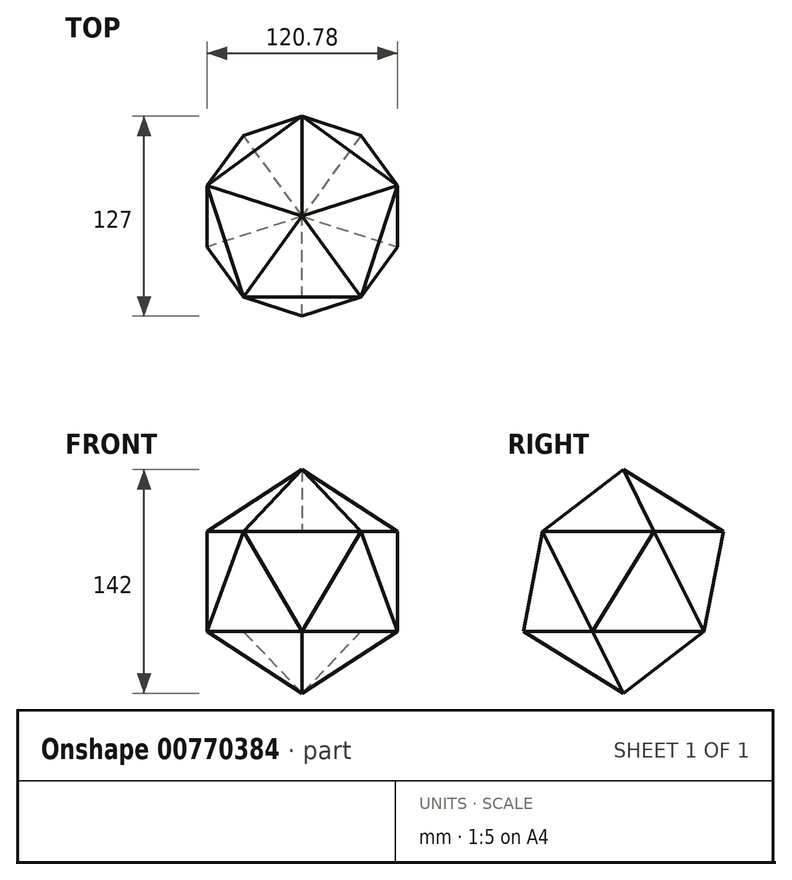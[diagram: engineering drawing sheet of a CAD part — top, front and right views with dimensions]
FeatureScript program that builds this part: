
annotation { "Feature Type Name" : "Feature", "Feature Type Description" : "" }
export const myFeature = defineFeature(function(context is Context, id is Id, definition is map)
    precondition{}
    {
        {
            var Q0;
            Q0=qCreatedBy(makeId("Top.planeOp"),FACE);
            var sketch = newSketch(context, id + "F0", { "sketchPlane" : qUnion([Q0])});
            skCircle(sketch, "E0", {"center": v(37.32, 51.37) * mm, "radius": 74.65 * mm});
            skCircle(sketch, "E1", {"center": v(-37.32, 51.37) * mm, "radius": 74.65 * mm});
            skCircle(sketch, "E2", {"center": v(0, 51.37) * mm, "radius": 64.65 * mm});
            skLineSegment(sketch, "E3", {"start": v(0, 0) * mm, "end": v(39.25, 0) * mm});
            skLineSegment(sketch, "E4", {"start": v(0, 63.5) * mm, "end": v(-63.5, 63.5) * mm});
            skCircle(sketch, "E5", {"center": v(0, 0) * mm, "radius": 63.5 * mm});
            skLineSegment(sketch, "E6", {"start": v(0, 0) * mm, "end": v(0, -63.5) * mm});
            skLineSegment(sketch, "E7", {"start": v(-37.32, 51.37) * mm, "end": v(37.32, 51.37) * mm});
            skLineSegment(sketch, "E8", {"start": v(37.32, 51.37) * mm, "end": v(60.4, -19.62) * mm});
            skLineSegment(sketch, "E9", {"start": v(60.4, -19.62) * mm, "end": v(0, -63.5) * mm});
            skLineSegment(sketch, "E10", {"start": v(0, -63.5) * mm, "end": v(-60.4, -19.62) * mm});
            skLineSegment(sketch, "E11", {"start": v(-60.4, -19.62) * mm, "end": v(-37.32, 51.37) * mm});
            skLineSegment(sketch, "E12", {"start": v(0, 63.5) * mm, "end": v(0, 116.02) * mm});
            skSolve(sketch);
        }
        {
            var Q0;
            Q0=sQuery(id+"F0.wireOp",EDGE,"E4");
            cPlane(context, id + "F1", {"entities" : qUnion([Q0]), "cplaneType" : CPlaneType.LINE_ANGLE, "offset" : 25.4 * mm, "angle" : 180 * degree, "width" : 152.4 * mm, "height" : 152.4 * mm});
        }
        {
            var Q0;
            Q0=qCreatedBy(id+"F1.planeOp",FACE);
            var sketch = newSketch(context, id + "F2", { "sketchPlane" : qUnion([Q0])});
            skLineSegment(sketch, "E13", {"start": v(63.5, 0) * mm, "end": v(0, 0) * mm});
            skLineSegment(sketch, "E14", {"start": v(31.75, 0) * mm, "end": v(63.5, 31.75) * mm});
            skLineSegment(sketch, "E15", {"start": v(31.75, 0) * mm, "end": v(0, -31.75) * mm});
            skLineSegment(sketch, "E16", {"start": v(63.5, 31.75) * mm, "end": v(0, 31.75) * mm});
            skLineSegment(sketch, "E17", {"start": v(0, -31.75) * mm, "end": v(63.5, -31.75) * mm});
            skLineSegment(sketch, "E18", {"start": v(0, 0) * mm, "end": v(0, 31.75) * mm});
            skLineSegment(sketch, "E19", {"start": v(0, 0) * mm, "end": v(0, -31.75) * mm});
            skSolve(sketch);
        }
        {
            var Q0;
            Q0=sQuery(id+"F2.wireOp",EDGE,"E16");
            cPlane(context, id + "F3", {"entities" : qUnion([Q0]), "cplaneType" : CPlaneType.LINE_ANGLE, "offset" : 25.4 * mm, "angle" : 270 * degree, "width" : 152.4 * mm, "height" : 152.4 * mm});
        }
        {
            var Q0;
            Q0=qCreatedBy(id+"F3.planeOp",FACE);
            var sketch = newSketch(context, id + "F4", { "sketchPlane" : qUnion([Q0])});
            skCircle(sketch, "E20.0", {"center": v(0, 0) * mm, "radius": 63.5 * mm});
            skLineSegment(sketch, "E21", {"start": v(-37.32, 51.37) * mm, "end": v(37.32, 51.37) * mm});
            skLineSegment(sketch, "E22", {"start": v(37.32, 51.37) * mm, "end": v(60.4, -19.62) * mm});
            skLineSegment(sketch, "E23", {"start": v(60.4, -19.62) * mm, "end": v(0, -63.5) * mm});
            skLineSegment(sketch, "E24", {"start": v(0, -63.5) * mm, "end": v(-60.4, -19.62) * mm});
            skLineSegment(sketch, "E25", {"start": v(-60.4, -19.62) * mm, "end": v(-37.32, 51.37) * mm});
            skLineSegment(sketch, "E26", {"start": v(0, 51.37) * mm, "end": v(0, 63.5) * mm});
            skLineSegment(sketch, "E27", {"start": v(30.2, -41.56) * mm, "end": v(37.32, -51.37) * mm});
            skLineSegment(sketch, "E28", {"start": v(37.32, -51.37) * mm, "end": v(60.4, -19.62) * mm});
            skLineSegment(sketch, "E29", {"start": v(37.32, -51.37) * mm, "end": v(0, -63.5) * mm});
            skLineSegment(sketch, "E30", {"start": v(-30.2, -41.56) * mm, "end": v(-37.32, -51.37) * mm});
            skLineSegment(sketch, "E31", {"start": v(-37.32, -51.37) * mm, "end": v(0, -63.5) * mm});
            skLineSegment(sketch, "E32", {"start": v(-37.32, -51.37) * mm, "end": v(-60.4, -19.62) * mm});
            skLineSegment(sketch, "E33", {"start": v(-48.86, 15.87) * mm, "end": v(-60.4, 19.62) * mm});
            skLineSegment(sketch, "E34", {"start": v(-60.4, 19.62) * mm, "end": v(-60.4, -19.62) * mm});
            skLineSegment(sketch, "E35", {"start": v(-60.4, 19.62) * mm, "end": v(-37.32, 51.37) * mm});
            skLineSegment(sketch, "E36", {"start": v(-37.32, 51.37) * mm, "end": v(0, 63.5) * mm});
            skLineSegment(sketch, "E37", {"start": v(0, 63.5) * mm, "end": v(37.32, 51.37) * mm});
            skLineSegment(sketch, "E38", {"start": v(60.4, 19.62) * mm, "end": v(37.32, 51.37) * mm});
            skLineSegment(sketch, "E39", {"start": v(60.4, 19.62) * mm, "end": v(60.4, -19.62) * mm});
            skLineSegment(sketch, "E40", {"start": v(48.86, 15.87) * mm, "end": v(60.4, 19.62) * mm});
            skLineSegment(sketch, "E41", {"start": v(0, 0) * mm, "end": v(30.2, -41.56) * mm});
            skLineSegment(sketch, "E42", {"start": v(0, 0) * mm, "end": v(-30.2, -41.56) * mm});
            skLineSegment(sketch, "E43", {"start": v(0, 0) * mm, "end": v(-48.86, 15.87) * mm});
            skLineSegment(sketch, "E44", {"start": v(0, 0) * mm, "end": v(48.86, 15.87) * mm});
            skLineSegment(sketch, "E45", {"start": v(0, 0) * mm, "end": v(0, 51.37) * mm});
            skSolve(sketch);
        }
        {
            var Q0;
            Q0=sQuery(id+"F2.wireOp",EDGE,"E17");
            cPlane(context, id + "F5", {"entities" : qUnion([Q0]), "cplaneType" : CPlaneType.LINE_ANGLE, "offset" : 25.4 * mm, "angle" : 90 * degree, "width" : 152.4 * mm, "height" : 152.4 * mm});
        }
        {
            var Q0;
            Q0=qCreatedBy(id+"F5.planeOp",FACE);
            var sketch = newSketch(context, id + "F6", { "sketchPlane" : qUnion([Q0])});
            skCircle(sketch, "E46.0", {"center": v(0, 0) * mm, "radius": 63.5 * mm});
            skLineSegment(sketch, "E47", {"start": v(-37.32, 51.37) * mm, "end": v(37.32, 51.37) * mm});
            skLineSegment(sketch, "E48", {"start": v(37.32, 51.37) * mm, "end": v(60.4, -19.62) * mm});
            skLineSegment(sketch, "E49", {"start": v(60.4, -19.62) * mm, "end": v(0, -63.5) * mm});
            skLineSegment(sketch, "E50", {"start": v(0, -63.5) * mm, "end": v(-60.4, -19.62) * mm});
            skLineSegment(sketch, "E51", {"start": v(-60.4, -19.62) * mm, "end": v(-37.32, 51.37) * mm});
            skLineSegment(sketch, "E52", {"start": v(0, 51.37) * mm, "end": v(0, 63.5) * mm});
            skLineSegment(sketch, "E53", {"start": v(30.2, -41.56) * mm, "end": v(37.32, -51.37) * mm});
            skLineSegment(sketch, "E54", {"start": v(37.32, -51.37) * mm, "end": v(60.4, -19.62) * mm});
            skLineSegment(sketch, "E55", {"start": v(37.32, -51.37) * mm, "end": v(0, -63.5) * mm});
            skLineSegment(sketch, "E56", {"start": v(-30.2, -41.56) * mm, "end": v(-37.32, -51.37) * mm});
            skLineSegment(sketch, "E57", {"start": v(-37.32, -51.37) * mm, "end": v(0, -63.5) * mm});
            skLineSegment(sketch, "E58", {"start": v(-37.32, -51.37) * mm, "end": v(-60.4, -19.62) * mm});
            skLineSegment(sketch, "E59", {"start": v(-48.86, 15.87) * mm, "end": v(-60.4, 19.62) * mm});
            skLineSegment(sketch, "E60", {"start": v(-60.4, 19.62) * mm, "end": v(-60.4, -19.62) * mm});
            skLineSegment(sketch, "E61", {"start": v(-60.4, 19.62) * mm, "end": v(-37.32, 51.37) * mm});
            skLineSegment(sketch, "E62", {"start": v(-37.32, 51.37) * mm, "end": v(0, 63.5) * mm});
            skLineSegment(sketch, "E63", {"start": v(0, 63.5) * mm, "end": v(37.32, 51.37) * mm});
            skLineSegment(sketch, "E64", {"start": v(60.4, 19.62) * mm, "end": v(37.32, 51.37) * mm});
            skLineSegment(sketch, "E65", {"start": v(60.4, 19.62) * mm, "end": v(60.4, -19.62) * mm});
            skLineSegment(sketch, "E66", {"start": v(48.86, 15.87) * mm, "end": v(60.4, 19.62) * mm});
            skLineSegment(sketch, "E67", {"start": v(0, 0) * mm, "end": v(30.2, -41.56) * mm});
            skLineSegment(sketch, "E68", {"start": v(0, 0) * mm, "end": v(-30.2, -41.56) * mm});
            skLineSegment(sketch, "E69", {"start": v(0, 0) * mm, "end": v(-48.86, 15.88) * mm});
            skLineSegment(sketch, "E70", {"start": v(0, 0) * mm, "end": v(48.86, 15.87) * mm});
            skLineSegment(sketch, "E71", {"start": v(0, 0) * mm, "end": v(0, 51.37) * mm});
            skLineSegment(sketch, "E72.0", {"start": v(-60.4, -19.62) * mm, "end": v(-60.4, 19.62) * mm, "construction": true});
            skLineSegment(sketch, "E73", {"start": v(63.5, 0) * mm, "end": v(74.27, 0) * mm});
            skPoint(sketch, "E73.startSnap0", {"position": v(60.4, 0) * mm});
            skSolve(sketch);
        }
        {
            var Q0;
            Q0=qCreatedBy(makeId("Front.planeOp"),FACE);
            var sketch = newSketch(context, id + "F7", { "sketchPlane" : qUnion([Q0])});
            skLineSegment(sketch, "E74", {"start": v(39.25, 31.75) * mm, "end": v(0, 31.75) * mm});
            skLineSegment(sketch, "E75", {"start": v(39.25, 31.75) * mm, "end": v(0, 71) * mm});
            skLineSegment(sketch, "E76", {"start": v(0, -31.75) * mm, "end": v(39.25, -31.75) * mm});
            skLineSegment(sketch, "E77", {"start": v(39.25, -31.75) * mm, "end": v(0, -71) * mm});
            skLineSegment(sketch, "E78", {"start": v(39.25, -31.75) * mm, "end": v(63.5, -31.75) * mm});
            skLineSegment(sketch, "E79", {"start": v(63.5, -31.75) * mm, "end": v(0, 0) * mm});
            skCircle(sketch, "E80", {"center": v(0, 0) * mm, "radius": 71 * mm});
            skLineSegment(sketch, "E81", {"start": v(0, 0) * mm, "end": v(0, -71) * mm});
            skLineSegment(sketch, "E82", {"start": v(0, 0) * mm, "end": v(0, 71) * mm});
            skLineSegment(sketch, "E83", {"start": v(39.25, 31.75) * mm, "end": v(71, 0) * mm});
            skLineSegment(sketch, "E84", {"start": v(0, 0) * mm, "end": v(39.25, 0) * mm});
            skLineSegment(sketch, "E85", {"start": v(39.25, 0) * mm, "end": v(39.25, 31.75) * mm});
            skSolve(sketch);
        }
        {
            var Q0;
            Q0=qCreatedBy(makeId("Top.planeOp"),FACE);
            var sketch = newSketch(context, id + "F8", { "sketchPlane" : qUnion([Q0])});
            skLineSegment(sketch, "E86", {"start": v(0, 0) * mm, "end": v(71, 0) * mm});
            skCircle(sketch, "E87", {"center": v(0, 0) * mm, "radius": 71 * mm});
            skLineSegment(sketch, "E88", {"start": v(0, 0) * mm, "end": v(67.52, -21.94) * mm});
            skLineSegment(sketch, "E89", {"start": v(0, 0) * mm, "end": v(67.52, 21.94) * mm});
            skLineSegment(sketch, "E90", {"start": v(0, 0) * mm, "end": v(41.73, 57.44) * mm});
            skLineSegment(sketch, "E91", {"start": v(0, 0) * mm, "end": v(0, 71) * mm});
            skLineSegment(sketch, "E92", {"start": v(0, 0) * mm, "end": v(41.73, -57.44) * mm});
            skLineSegment(sketch, "E93", {"start": v(0, 0) * mm, "end": v(0, -71) * mm});
            skLineSegment(sketch, "E94", {"start": v(0, 0) * mm, "end": v(-41.73, -57.44) * mm});
            skLineSegment(sketch, "E95", {"start": v(0, 0) * mm, "end": v(-41.73, 57.44) * mm});
            skLineSegment(sketch, "E96", {"start": v(0, 0) * mm, "end": v(-67.52, 21.94) * mm});
            skLineSegment(sketch, "E97", {"start": v(0, 0) * mm, "end": v(-67.52, -21.94) * mm});
            skSolve(sketch);
        }
        {
            var Q0;
            {var subQ0=sQuery(id+"F7.wireOp",EDGE,"E81");var subQ1=makeQuery(id+"F7.imprint","INTERSECT",VERTEX,{"derivedFrom":[sQuery(id+"F7.wireOp",EDGE,"E76"),subQ0]});Q0=makeQuery(id+"F7.imprint","IMPRINT",FACE,{"disambiguationData":[TD([[makeQuery(id+"F7.imprint","IMPRINT",EDGE,{"disambiguationData":[TD([[subQ1,1.0]])],"derivedFrom":subQ0}),-1.0]])]});}
            var Q1;
            Q1=sQuery(id+"F7.wireOp",EDGE,"E81");
            revolve(context, id + "F9", {"surfaceOperationType" : NewSurfaceOperationType.NEW, "entities" : qUnion([Q0]), "axis" : qUnion([Q1]), "revolveType" : RevolveType.FULL});
        }
        {
            var Q0;
            Q0=sQuery(id+"F6.wireOp",VERTEX,"E53.end");
            var Q1;
            Q1=sQuery(id+"F6.wireOp",VERTEX,"E67.start");
            var Q2;
            Q2=sQuery(id+"F7.wireOp",VERTEX,"E77.end");
            cPlane(context, id + "F10", {"entities" : qUnion([Q0, Q1, Q2]), "cplaneType" : CPlaneType.THREE_POINT, "offset" : 25.4 * mm, "width" : 152.4 * mm, "height" : 152.4 * mm});
        }
        {
            var Q0;
            Q0=qCreatedBy(id+"F10.planeOp",FACE);
            var sketch = newSketch(context, id + "F11", { "sketchPlane" : qUnion([Q0])});
            skLineSegment(sketch, "E98", {"start": v(0, -71) * mm, "end": v(-51.37, -31.75) * mm});
            skLineSegment(sketch, "E99", {"start": v(-51.37, -31.75) * mm, "end": v(-63.5, -31.75) * mm});
            skLineSegment(sketch, "E100", {"start": v(-63.5, -31.75) * mm, "end": v(-63.5, -71) * mm});
            skLineSegment(sketch, "E101", {"start": v(-63.5, -71) * mm, "end": v(0, -71) * mm});
            skSolve(sketch);
        }
        {
            var Q0;
            {var subQ0=sQuery(id+"F11.wireOp",EDGE,"E98");Q0=makeQuery(id+"F11.imprint","IMPRINT",FACE,{"disambiguationData":[TD([[makeQuery(id+"F11.imprint","IMPRINT",EDGE,{"derivedFrom":subQ0}),1.0]])]});}
            var Q1;
            Q1=sQuery(id+"F6.wireOp",VERTEX,"E48.end");
            var Q2;
            Q2=sQuery(id+"F6.wireOp",VERTEX,"E49.end");
            extrude(context, id + "F12", {"entities" : qUnion([Q0]), "operationType" : NewBodyOperationType.REMOVE, "endBound" : BoundingType.UP_TO_VERTEX, "depth" : 25.4 * mm, "endBoundEntityVertex" : qUnion([Q1]), "offsetDistance" : 25.4 * mm, "hasSecondDirection" : true, "secondDirectionBound" : SecondDirectionBoundingType.UP_TO_VERTEX, "secondDirectionOppositeDirection" : true, "secondDirectionDepth" : 25.4 * mm, "secondDirectionBoundEntityVertex" : qUnion([Q2])});
        }
        {
            var Q0;
            Q0=sQuery(id+"F7.wireOp",VERTEX,"E77.end");
            var Q1;
            Q1=sQuery(id+"F6.wireOp",VERTEX,"E67.start");
            var Q2;
            Q2=sQuery(id+"F6.wireOp",VERTEX,"E56.end");
            cPlane(context, id + "F13", {"entities" : qUnion([Q0, Q1, Q2]), "cplaneType" : CPlaneType.THREE_POINT, "offset" : 25.4 * mm, "width" : 152.4 * mm, "height" : 152.4 * mm});
        }
        {
            var Q0;
            Q0=qCreatedBy(id+"F13.planeOp",FACE);
            var sketch = newSketch(context, id + "F14", { "sketchPlane" : qUnion([Q0])});
            skLineSegment(sketch, "E102", {"start": v(0, -71) * mm, "end": v(51.37, -31.75) * mm});
            skLineSegment(sketch, "E103", {"start": v(0, -71) * mm, "end": v(63.5, -71) * mm});
            skLineSegment(sketch, "E104", {"start": v(63.5, -71) * mm, "end": v(63.5, -31.75) * mm});
            skLineSegment(sketch, "E105", {"start": v(63.5, -31.75) * mm, "end": v(51.37, -31.75) * mm});
            skSolve(sketch);
        }
        {
            var Q0;
            {var subQ0=sQuery(id+"F14.wireOp",EDGE,"E102");Q0=makeQuery(id+"F14.imprint","IMPRINT",FACE,{"disambiguationData":[TD([[makeQuery(id+"F14.imprint","IMPRINT",EDGE,{"derivedFrom":subQ0}),-1.0]])]});}
            var Q1;
            Q1=sQuery(id+"F6.wireOp",VERTEX,"E49.end");
            var Q2;
            Q2=sQuery(id+"F6.wireOp",VERTEX,"E50.end");
            extrude(context, id + "F15", {"entities" : qUnion([Q0]), "operationType" : NewBodyOperationType.REMOVE, "endBound" : BoundingType.UP_TO_VERTEX, "oppositeDirection" : true, "depth" : 25.4 * mm, "endBoundEntityVertex" : qUnion([Q1]), "offsetDistance" : 25.4 * mm, "hasSecondDirection" : true, "secondDirectionBound" : SecondDirectionBoundingType.UP_TO_VERTEX, "secondDirectionOppositeDirection" : false, "secondDirectionDepth" : 25.4 * mm, "secondDirectionBoundEntityVertex" : qUnion([Q2])});
        }
        {
            var Q0;
            Q0=sQuery(id+"F6.wireOp",VERTEX,"E67.start");
            var Q1;
            Q1=sQuery(id+"F7.wireOp",VERTEX,"E77.end");
            var Q2;
            Q2=sQuery(id+"F6.wireOp",VERTEX,"E59.end");
            cPlane(context, id + "F16", {"entities" : qUnion([Q0, Q1, Q2]), "cplaneType" : CPlaneType.THREE_POINT, "offset" : 25.4 * mm, "width" : 152.4 * mm, "height" : 152.4 * mm});
        }
        {
            var Q0;
            Q0=qCreatedBy(id+"F16.planeOp",FACE);
            var sketch = newSketch(context, id + "F17", { "sketchPlane" : qUnion([Q0])});
            skLineSegment(sketch, "E106", {"start": v(0, -71) * mm, "end": v(-51.37, -31.75) * mm});
            skLineSegment(sketch, "E107", {"start": v(0, -71) * mm, "end": v(-63.5, -71) * mm});
            skLineSegment(sketch, "E108", {"start": v(-63.5, -71) * mm, "end": v(-63.5, -31.75) * mm});
            skLineSegment(sketch, "E109", {"start": v(-63.5, -31.75) * mm, "end": v(-51.37, -31.75) * mm});
            skSolve(sketch);
        }
        {
            var Q0;
            {var subQ0=sQuery(id+"F17.wireOp",EDGE,"E106");Q0=makeQuery(id+"F17.imprint","IMPRINT",FACE,{"disambiguationData":[TD([[makeQuery(id+"F17.imprint","IMPRINT",EDGE,{"derivedFrom":subQ0}),1.0]])]});}
            var Q1;
            Q1=sQuery(id+"F6.wireOp",VERTEX,"E47.start");
            var Q2;
            Q2=sQuery(id+"F6.wireOp",VERTEX,"E50.end");
            extrude(context, id + "F18", {"entities" : qUnion([Q0]), "operationType" : NewBodyOperationType.REMOVE, "endBound" : BoundingType.UP_TO_VERTEX, "oppositeDirection" : true, "depth" : 25.4 * mm, "endBoundEntityVertex" : qUnion([Q1]), "offsetDistance" : 25.4 * mm, "hasSecondDirection" : true, "secondDirectionBound" : SecondDirectionBoundingType.UP_TO_VERTEX, "secondDirectionOppositeDirection" : false, "secondDirectionDepth" : 25.4 * mm, "secondDirectionBoundEntityVertex" : qUnion([Q2])});
        }
        {
            var Q0;
            Q0=sQuery(id+"F7.wireOp",VERTEX,"E77.end");
            var Q1;
            Q1=sQuery(id+"F6.wireOp",VERTEX,"E67.start");
            var Q2;
            Q2=sQuery(id+"F6.wireOp",VERTEX,"E52.end");
            cPlane(context, id + "F19", {"entities" : qUnion([Q0, Q1, Q2]), "cplaneType" : CPlaneType.THREE_POINT, "offset" : 25.4 * mm, "width" : 152.4 * mm, "height" : 152.4 * mm});
        }
        {
            var Q0;
            Q0=qCreatedBy(id+"F19.planeOp",FACE);
            var sketch = newSketch(context, id + "F20", { "sketchPlane" : qUnion([Q0])});
            skLineSegment(sketch, "E110", {"start": v(0, -71) * mm, "end": v(51.37, -31.75) * mm});
            skLineSegment(sketch, "E111", {"start": v(0, -71) * mm, "end": v(63.5, -71) * mm});
            skLineSegment(sketch, "E112", {"start": v(63.5, -71) * mm, "end": v(63.5, -31.75) * mm});
            skLineSegment(sketch, "E113", {"start": v(63.5, -31.75) * mm, "end": v(51.37, -31.75) * mm});
            skSolve(sketch);
        }
        {
            var Q0;
            {var subQ0=sQuery(id+"F20.wireOp",EDGE,"E110");Q0=makeQuery(id+"F20.imprint","IMPRINT",FACE,{"disambiguationData":[TD([[makeQuery(id+"F20.imprint","IMPRINT",EDGE,{"derivedFrom":subQ0}),-1.0]])]});}
            var Q1;
            Q1=sQuery(id+"F6.wireOp",VERTEX,"E47.start");
            var Q2;
            Q2=sQuery(id+"F6.wireOp",VERTEX,"E47.end");
            extrude(context, id + "F21", {"entities" : qUnion([Q0]), "operationType" : NewBodyOperationType.REMOVE, "endBound" : BoundingType.UP_TO_VERTEX, "oppositeDirection" : true, "depth" : 25.4 * mm, "endBoundEntityVertex" : qUnion([Q1]), "offsetDistance" : 25.4 * mm, "hasSecondDirection" : true, "secondDirectionBound" : SecondDirectionBoundingType.UP_TO_VERTEX, "secondDirectionOppositeDirection" : false, "secondDirectionDepth" : 25.4 * mm, "secondDirectionBoundEntityVertex" : qUnion([Q2])});
        }
        {
            var Q0;
            Q0=sQuery(id+"F6.wireOp",VERTEX,"E64.start");
            var Q1;
            Q1=sQuery(id+"F6.wireOp",VERTEX,"E67.start");
            var Q2;
            Q2=sQuery(id+"F7.wireOp",VERTEX,"E77.end");
            cPlane(context, id + "F22", {"entities" : qUnion([Q0, Q1, Q2]), "cplaneType" : CPlaneType.THREE_POINT, "offset" : 25.4 * mm, "width" : 152.4 * mm, "height" : 152.4 * mm});
        }
        {
            var Q0;
            Q0=qCreatedBy(id+"F22.planeOp",FACE);
            var sketch = newSketch(context, id + "F23", { "sketchPlane" : qUnion([Q0])});
            skLineSegment(sketch, "E114", {"start": v(0, -71) * mm, "end": v(-51.37, -31.75) * mm});
            skLineSegment(sketch, "E115", {"start": v(-51.37, -31.75) * mm, "end": v(-63.5, -31.75) * mm});
            skLineSegment(sketch, "E116", {"start": v(-63.5, -31.75) * mm, "end": v(-63.5, -71) * mm});
            skLineSegment(sketch, "E117", {"start": v(-63.5, -71) * mm, "end": v(0, -71) * mm});
            skSolve(sketch);
        }
        {
            var Q0;
            {var subQ0=sQuery(id+"F23.wireOp",EDGE,"E114");Q0=makeQuery(id+"F23.imprint","IMPRINT",FACE,{"disambiguationData":[TD([[makeQuery(id+"F23.imprint","IMPRINT",EDGE,{"derivedFrom":subQ0}),1.0]])]});}
            var Q1;
            Q1=sQuery(id+"F6.wireOp",VERTEX,"E47.end");
            var Q2;
            Q2=sQuery(id+"F6.wireOp",VERTEX,"E48.end");
            extrude(context, id + "F24", {"entities" : qUnion([Q0]), "operationType" : NewBodyOperationType.REMOVE, "endBound" : BoundingType.UP_TO_VERTEX, "depth" : 25.4 * mm, "endBoundEntityVertex" : qUnion([Q1]), "offsetDistance" : 25.4 * mm, "hasSecondDirection" : true, "secondDirectionBound" : SecondDirectionBoundingType.UP_TO_VERTEX, "secondDirectionOppositeDirection" : true, "secondDirectionDepth" : 25.4 * mm, "secondDirectionBoundEntityVertex" : qUnion([Q2])});
        }
        {
            var Q0;
            Q0=sQuery(id+"F6.wireOp",EDGE,"E49");
            cPoint(context, id + "F25", {"entities" : qUnion([Q0]), "parameter" : 0.5});
        }
        {
            var Q0;
            Q0 = qCreatedBy(id + "F25" ,VERTEX);
            var Q1;
            Q1=sQuery(id+"F6.wireOp",VERTEX,"E53.end");
            var Q2;
            Q2=sQuery(id+"F4.wireOp",VERTEX,"E21.end");
            cPlane(context, id + "F26", {"entities" : qUnion([Q0, Q1, Q2]), "cplaneType" : CPlaneType.THREE_POINT, "offset" : 25.4 * mm, "width" : 152.4 * mm, "height" : 152.4 * mm});
        }
        {
            var Q0;
            Q0=qCreatedBy(id+"F26.planeOp",FACE);
            var sketch = newSketch(context, id + "F27", { "sketchPlane" : qUnion([Q0])});
            skLineSegment(sketch, "E118.bottom", {"start": v(-51.37, -31.75) * mm, "end": v(-71, -31.75) * mm});
            skLineSegment(sketch, "E118.top", {"start": v(-51.37, 31.75) * mm, "end": v(-71, 31.75) * mm});
            skLineSegment(sketch, "E118.left", {"start": v(-51.37, -31.75) * mm, "end": v(-51.37, 31.75) * mm});
            skLineSegment(sketch, "E118.right", {"start": v(-71, -31.75) * mm, "end": v(-71, 31.75) * mm});
            skLineSegment(sketch, "E119", {"start": v(-51.37, -31.75) * mm, "end": v(-63.5, 31.75) * mm});
            skSolve(sketch);
        }
        {
            var Q0;
            Q0=makeQuery(id+"F27.imprint","IMPRINT",FACE,{"disambiguationData":[TD([[makeQuery(id+"F27.imprint","IMPRINT",EDGE,{"derivedFrom":sQuery(id+"F27.wireOp",EDGE,"E118.bottom")}),-1.0]])]});
            var Q1;
            Q1=sQuery(id+"F6.wireOp",VERTEX,"E48.end");
            var Q2;
            Q2=sQuery(id+"F6.wireOp",VERTEX,"E49.end");
            extrude(context, id + "F28", {"entities" : qUnion([Q0]), "operationType" : NewBodyOperationType.REMOVE, "endBound" : BoundingType.THROUGH_ALL, "depth" : 25.4 * mm, "endBoundEntityVertex" : qUnion([Q1]), "offsetDistance" : 25.4 * mm, "hasSecondDirection" : true, "secondDirectionBound" : SecondDirectionBoundingType.THROUGH_ALL, "secondDirectionOppositeDirection" : true, "secondDirectionDepth" : 25.4 * mm, "secondDirectionBoundEntityVertex" : qUnion([Q2])});
        }
        {
            var Q0;
            Q0=sQuery(id+"F4.wireOp",EDGE,"E22");
            cPoint(context, id + "F29", {"entities" : qUnion([Q0]), "parameter" : 0.5});
        }
        {
            var Q0;
            Q0=sQuery(id+"F6.wireOp",VERTEX,"E48.end");
            var Q1;
            Q1 = qCreatedBy(id + "F29" ,VERTEX);
            var Q2;
            Q2=sQuery(id+"F4.wireOp",VERTEX,"E38.start");
            cPlane(context, id + "F30", {"entities" : qUnion([Q0, Q1, Q2]), "cplaneType" : CPlaneType.THREE_POINT, "offset" : 25.4 * mm, "width" : 152.4 * mm, "height" : 152.4 * mm});
        }
        {
            var Q0;
            Q0=qCreatedBy(id+"F30.planeOp",FACE);
            var sketch = newSketch(context, id + "F31", { "sketchPlane" : qUnion([Q0])});
            skLineSegment(sketch, "E120.bottom", {"start": v(51.37, 31.75) * mm, "end": v(71, 31.75) * mm});
            skLineSegment(sketch, "E120.top", {"start": v(51.37, -31.75) * mm, "end": v(71, -31.75) * mm});
            skLineSegment(sketch, "E120.left", {"start": v(51.37, 31.75) * mm, "end": v(51.37, -31.75) * mm});
            skLineSegment(sketch, "E120.right", {"start": v(71, 31.75) * mm, "end": v(71, -31.75) * mm});
            skLineSegment(sketch, "E121", {"start": v(51.37, 31.75) * mm, "end": v(63.5, -31.75) * mm});
            skSolve(sketch);
        }
        {
            var Q0;
            Q0=makeQuery(id+"F58.imprint","IMPRINT",FACE,{"disambiguationData":[TD([[makeQuery(id+"F58.imprint","IMPRINT",EDGE,{"derivedFrom":sQuery(id+"F58.wireOp",EDGE,"E136.bottom")}),-1.0]])]});
            var Q1;
            Q1=makeQuery(id+"F31.imprint","IMPRINT",FACE,{"disambiguationData":[TD([[makeQuery(id+"F31.imprint","IMPRINT",EDGE,{"derivedFrom":sQuery(id+"F31.wireOp",EDGE,"E120.bottom")}),-1.0]])]});
            extrude(context, id + "F32", {"entities" : qUnion([Q0, Q1]), "operationType" : NewBodyOperationType.REMOVE, "endBound" : BoundingType.THROUGH_ALL, "oppositeDirection" : true, "depth" : 25.4 * mm, "offsetDistance" : 25.4 * mm, "hasSecondDirection" : true, "secondDirectionBound" : SecondDirectionBoundingType.THROUGH_ALL, "secondDirectionOppositeDirection" : false, "secondDirectionDepth" : 25.4 * mm});
        }
        {
            var Q0;
            Q0=sQuery(id+"F6.wireOp",VERTEX,"E64.start");
            var Q1;
            Q1=sQuery(id+"F6.wireOp",VERTEX,"E66.start");
            var Q2;
            Q2=sQuery(id+"F4.wireOp",VERTEX,"E22.end");
            cPlane(context, id + "F33", {"entities" : qUnion([Q0, Q1, Q2]), "cplaneType" : CPlaneType.THREE_POINT, "offset" : 25.4 * mm, "width" : 152.4 * mm, "height" : 152.4 * mm});
        }
        {
            var Q0;
            Q0=qCreatedBy(id+"F33.planeOp",FACE);
            var sketch = newSketch(context, id + "F34", { "sketchPlane" : qUnion([Q0])});
            skLineSegment(sketch, "E122.bottom", {"start": v(51.37, -31.75) * mm, "end": v(71, -31.75) * mm});
            skLineSegment(sketch, "E122.top", {"start": v(51.37, 31.75) * mm, "end": v(71, 31.75) * mm});
            skLineSegment(sketch, "E122.left", {"start": v(51.37, -31.75) * mm, "end": v(51.37, 31.75) * mm});
            skLineSegment(sketch, "E122.right", {"start": v(71, -31.75) * mm, "end": v(71, 31.75) * mm});
            skLineSegment(sketch, "E123", {"start": v(51.37, -31.75) * mm, "end": v(63.5, 31.75) * mm});
            skSolve(sketch);
        }
        {
            var Q0;
            Q0=makeQuery(id+"F55.imprint","IMPRINT",FACE,{"disambiguationData":[TD([[makeQuery(id+"F55.imprint","IMPRINT",EDGE,{"derivedFrom":sQuery(id+"F55.wireOp",EDGE,"E134.bottom")}),-1.0]])]});
            var Q1;
            Q1=makeQuery(id+"F34.imprint","IMPRINT",FACE,{"disambiguationData":[TD([[makeQuery(id+"F34.imprint","IMPRINT",EDGE,{"derivedFrom":sQuery(id+"F34.wireOp",EDGE,"E122.bottom")}),1.0]])]});
            extrude(context, id + "F35", {"entities" : qUnion([Q0, Q1]), "operationType" : NewBodyOperationType.REMOVE, "endBound" : BoundingType.THROUGH_ALL, "oppositeDirection" : true, "depth" : 25.4 * mm, "offsetDistance" : 25.4 * mm, "hasSecondDirection" : true, "secondDirectionBound" : SecondDirectionBoundingType.THROUGH_ALL, "secondDirectionOppositeDirection" : false, "secondDirectionDepth" : 25.4 * mm});
        }
        {
            var Q0;
            Q0=sQuery(id+"F4.wireOp",EDGE,"E23");
            cPoint(context, id + "F36", {"entities" : qUnion([Q0]), "parameter" : 0.5});
        }
        {
            var Q0;
            Q0 = qCreatedBy(id + "F36" ,VERTEX);
            var Q1;
            Q1=sQuery(id+"F4.wireOp",VERTEX,"E27.end");
            var Q2;
            Q2=sQuery(id+"F6.wireOp",VERTEX,"E47.end");
            cPlane(context, id + "F37", {"entities" : qUnion([Q0, Q1, Q2]), "cplaneType" : CPlaneType.THREE_POINT, "offset" : 25.4 * mm, "width" : 152.4 * mm, "height" : 152.4 * mm});
        }
        {
            var Q0;
            Q0=qCreatedBy(id+"F37.planeOp",FACE);
            var sketch = newSketch(context, id + "F38", { "sketchPlane" : qUnion([Q0])});
            skLineSegment(sketch, "E124.bottom", {"start": v(51.37, 31.75) * mm, "end": v(71, 31.75) * mm});
            skLineSegment(sketch, "E124.top", {"start": v(51.37, -31.75) * mm, "end": v(71, -31.75) * mm});
            skLineSegment(sketch, "E124.left", {"start": v(51.37, 31.75) * mm, "end": v(51.37, -31.75) * mm});
            skLineSegment(sketch, "E124.right", {"start": v(71, 31.75) * mm, "end": v(71, -31.75) * mm});
            skLineSegment(sketch, "E125", {"start": v(51.37, 31.75) * mm, "end": v(63.5, -31.75) * mm});
            skSolve(sketch);
        }
        {
            var Q0;
            Q0=makeQuery(id+"F38.imprint","IMPRINT",FACE,{"disambiguationData":[TD([[makeQuery(id+"F38.imprint","IMPRINT",EDGE,{"derivedFrom":sQuery(id+"F38.wireOp",EDGE,"E124.bottom")}),-1.0]])]});
            extrude(context, id + "F39", {"entities" : qUnion([Q0]), "operationType" : NewBodyOperationType.REMOVE, "endBound" : BoundingType.THROUGH_ALL, "oppositeDirection" : true, "depth" : 25.4 * mm, "offsetDistance" : 25.4 * mm, "hasSecondDirection" : true, "secondDirectionBound" : SecondDirectionBoundingType.THROUGH_ALL, "secondDirectionOppositeDirection" : false, "secondDirectionDepth" : 25.4 * mm});
        }
        {
            var Q0;
            Q0=sQuery(id+"F6.wireOp",VERTEX,"E52.start");
            var Q1;
            Q1=sQuery(id+"F6.wireOp",VERTEX,"E52.end");
            var Q2;
            Q2=sQuery(id+"F4.wireOp",VERTEX,"E23.end");
            cPlane(context, id + "F40", {"entities" : qUnion([Q0, Q1, Q2]), "cplaneType" : CPlaneType.THREE_POINT, "offset" : 25.4 * mm, "width" : 152.4 * mm, "height" : 152.4 * mm});
        }
        {
            var Q0;
            Q0=qCreatedBy(id+"F40.planeOp",FACE);
            var sketch = newSketch(context, id + "F41", { "sketchPlane" : qUnion([Q0])});
            skLineSegment(sketch, "E126.bottom", {"start": v(-51.37, -31.75) * mm, "end": v(-71, -31.75) * mm});
            skLineSegment(sketch, "E126.top", {"start": v(-51.37, 31.75) * mm, "end": v(-71, 31.75) * mm});
            skLineSegment(sketch, "E126.left", {"start": v(-51.37, -31.75) * mm, "end": v(-51.37, 31.75) * mm});
            skLineSegment(sketch, "E126.right", {"start": v(-71, -31.75) * mm, "end": v(-71, 31.75) * mm});
            skLineSegment(sketch, "E127", {"start": v(-51.37, -31.75) * mm, "end": v(-63.5, 31.75) * mm});
            skSolve(sketch);
        }
        {
            var Q0;
            Q0=makeQuery(id+"F41.imprint","IMPRINT",FACE,{"disambiguationData":[TD([[makeQuery(id+"F41.imprint","IMPRINT",EDGE,{"derivedFrom":sQuery(id+"F41.wireOp",EDGE,"E126.bottom")}),-1.0]])]});
            extrude(context, id + "F42", {"entities" : qUnion([Q0]), "operationType" : NewBodyOperationType.REMOVE, "endBound" : BoundingType.THROUGH_ALL, "oppositeDirection" : true, "depth" : 25.4 * mm, "offsetDistance" : 25.4 * mm, "hasSecondDirection" : true, "secondDirectionBound" : SecondDirectionBoundingType.THROUGH_ALL, "secondDirectionOppositeDirection" : false, "secondDirectionDepth" : 25.4 * mm});
        }
        {
            var Q0;
            Q0=sQuery(id+"F4.wireOp",VERTEX,"E30.end");
            var Q1;
            Q1=sQuery(id+"F4.wireOp",VERTEX,"E30.start");
            var Q2;
            Q2=sQuery(id+"F6.wireOp",VERTEX,"E47.start");
            cPlane(context, id + "F43", {"entities" : qUnion([Q0, Q1, Q2]), "cplaneType" : CPlaneType.THREE_POINT, "offset" : 25.4 * mm, "width" : 152.4 * mm, "height" : 152.4 * mm});
        }
        {
            var Q0;
            Q0=qCreatedBy(id+"F43.planeOp",FACE);
            var sketch = newSketch(context, id + "F44", { "sketchPlane" : qUnion([Q0])});
            skLineSegment(sketch, "E128.bottom", {"start": v(-51.37, 31.75) * mm, "end": v(-71, 31.75) * mm});
            skLineSegment(sketch, "E128.top", {"start": v(-51.37, -31.75) * mm, "end": v(-71, -31.75) * mm});
            skLineSegment(sketch, "E128.left", {"start": v(-51.37, 31.75) * mm, "end": v(-51.37, -31.75) * mm});
            skLineSegment(sketch, "E128.right", {"start": v(-71, 31.75) * mm, "end": v(-71, -31.75) * mm});
            skLineSegment(sketch, "E129", {"start": v(-51.37, 31.75) * mm, "end": v(-63.5, -31.75) * mm});
            skSolve(sketch);
        }
        {
            var Q0;
            Q0=makeQuery(id+"F44.imprint","IMPRINT",FACE,{"disambiguationData":[TD([[makeQuery(id+"F44.imprint","IMPRINT",EDGE,{"derivedFrom":sQuery(id+"F44.wireOp",EDGE,"E128.bottom")}),1.0]])]});
            extrude(context, id + "F45", {"entities" : qUnion([Q0]), "operationType" : NewBodyOperationType.REMOVE, "endBound" : BoundingType.THROUGH_ALL, "oppositeDirection" : true, "depth" : 25.4 * mm, "offsetDistance" : 25.4 * mm, "hasSecondDirection" : true, "secondDirectionBound" : SecondDirectionBoundingType.THROUGH_ALL, "secondDirectionOppositeDirection" : false, "secondDirectionDepth" : 25.4 * mm});
        }
        {
            var Q0;
            Q0=sQuery(id+"F6.wireOp",VERTEX,"E59.start");
            var Q1;
            Q1=sQuery(id+"F6.wireOp",VERTEX,"E59.end");
            var Q2;
            Q2=sQuery(id+"F4.wireOp",VERTEX,"E24.end");
            cPlane(context, id + "F46", {"entities" : qUnion([Q0, Q1, Q2]), "cplaneType" : CPlaneType.THREE_POINT, "offset" : 25.4 * mm, "width" : 152.4 * mm, "height" : 152.4 * mm});
        }
        {
            var Q0;
            Q0=qCreatedBy(id+"F46.planeOp",FACE);
            var sketch = newSketch(context, id + "F47", { "sketchPlane" : qUnion([Q0])});
            skLineSegment(sketch, "E130.bottom", {"start": v(-51.37, -31.75) * mm, "end": v(-71, -31.75) * mm});
            skLineSegment(sketch, "E130.top", {"start": v(-51.37, 31.75) * mm, "end": v(-71, 31.75) * mm});
            skLineSegment(sketch, "E130.left", {"start": v(-51.37, -31.75) * mm, "end": v(-51.37, 31.75) * mm});
            skLineSegment(sketch, "E130.right", {"start": v(-71, -31.75) * mm, "end": v(-71, 31.75) * mm});
            skLineSegment(sketch, "E131", {"start": v(-51.37, -31.75) * mm, "end": v(-63.5, 31.75) * mm});
            skSolve(sketch);
        }
        {
            var Q0;
            Q0=makeQuery(id+"F47.imprint","IMPRINT",FACE,{"disambiguationData":[TD([[makeQuery(id+"F47.imprint","IMPRINT",EDGE,{"derivedFrom":sQuery(id+"F47.wireOp",EDGE,"E130.bottom")}),-1.0]])]});
            extrude(context, id + "F48", {"entities" : qUnion([Q0]), "operationType" : NewBodyOperationType.REMOVE, "endBound" : BoundingType.THROUGH_ALL, "oppositeDirection" : true, "depth" : 25.4 * mm, "offsetDistance" : 25.4 * mm, "hasSecondDirection" : true, "secondDirectionBound" : SecondDirectionBoundingType.THROUGH_ALL, "secondDirectionOppositeDirection" : false, "secondDirectionDepth" : 25.4 * mm});
        }
        {
            var Q0;
            Q0=sQuery(id+"F4.wireOp",EDGE,"E25");
            cPoint(context, id + "F49", {"entities" : qUnion([Q0]), "parameter" : 0.5});
        }
        {
            var Q0;
            Q0=sQuery(id+"F6.wireOp",VERTEX,"E50.end");
            var Q1;
            Q1 = qCreatedBy(id + "F49" ,VERTEX);
            var Q2;
            Q2=sQuery(id+"F4.wireOp",VERTEX,"E33.end");
            cPlane(context, id + "F50", {"entities" : qUnion([Q0, Q1, Q2]), "cplaneType" : CPlaneType.THREE_POINT, "offset" : 25.4 * mm, "width" : 152.4 * mm, "height" : 152.4 * mm});
        }
        {
            var Q0;
            Q0=qCreatedBy(id+"F50.planeOp",FACE);
            var sketch = newSketch(context, id + "F51", { "sketchPlane" : qUnion([Q0])});
            skLineSegment(sketch, "E132.bottom", {"start": v(51.37, 31.75) * mm, "end": v(71, 31.75) * mm});
            skLineSegment(sketch, "E132.top", {"start": v(51.37, -31.75) * mm, "end": v(71, -31.75) * mm});
            skLineSegment(sketch, "E132.left", {"start": v(51.37, 31.75) * mm, "end": v(51.37, -31.75) * mm});
            skLineSegment(sketch, "E132.right", {"start": v(71, 31.75) * mm, "end": v(71, -31.75) * mm});
            skLineSegment(sketch, "E133", {"start": v(51.37, 31.75) * mm, "end": v(63.5, -31.75) * mm});
            skSolve(sketch);
        }
        {
            var Q0;
            Q0=makeQuery(id+"F51.imprint","IMPRINT",FACE,{"disambiguationData":[TD([[makeQuery(id+"F51.imprint","IMPRINT",EDGE,{"derivedFrom":sQuery(id+"F51.wireOp",EDGE,"E132.bottom")}),-1.0]])]});
            extrude(context, id + "F52", {"entities" : qUnion([Q0]), "operationType" : NewBodyOperationType.REMOVE, "endBound" : BoundingType.THROUGH_ALL, "oppositeDirection" : true, "depth" : 25.4 * mm, "offsetDistance" : 25.4 * mm, "hasSecondDirection" : true, "secondDirectionBound" : SecondDirectionBoundingType.THROUGH_ALL, "secondDirectionOppositeDirection" : false, "secondDirectionDepth" : 25.4 * mm});
        }
        {
            var Q0;
            Q0=sQuery(id+"F6.wireOp",EDGE,"E50");
            cPoint(context, id + "F53", {"entities" : qUnion([Q0]), "parameter" : 0.5});
        }
        {
            var Q0;
            Q0 = qCreatedBy(id + "F53" ,VERTEX);
            var Q1;
            Q1=sQuery(id+"F6.wireOp",VERTEX,"E56.end");
            var Q2;
            Q2=sQuery(id+"F4.wireOp",VERTEX,"E21.start");
            cPlane(context, id + "F54", {"entities" : qUnion([Q0, Q1, Q2]), "cplaneType" : CPlaneType.THREE_POINT, "offset" : 25.4 * mm, "width" : 152.4 * mm, "height" : 152.4 * mm});
        }
        {
            var Q0;
            Q0=qCreatedBy(id+"F54.planeOp",FACE);
            var sketch = newSketch(context, id + "F55", { "sketchPlane" : qUnion([Q0])});
            skLineSegment(sketch, "E134.bottom", {"start": v(-51.37, -31.75) * mm, "end": v(-71, -31.75) * mm});
            skLineSegment(sketch, "E134.top", {"start": v(-51.37, 31.75) * mm, "end": v(-71, 31.75) * mm});
            skLineSegment(sketch, "E134.left", {"start": v(-51.37, -31.75) * mm, "end": v(-51.37, 31.75) * mm});
            skLineSegment(sketch, "E134.right", {"start": v(-71, -31.75) * mm, "end": v(-71, 31.75) * mm});
            skLineSegment(sketch, "E135", {"start": v(-51.37, -31.75) * mm, "end": v(-63.5, 31.75) * mm});
            skSolve(sketch);
        }
        {
            var Q0;
            Q0=makeQuery(id+"F55.imprint","IMPRINT",FACE,{"disambiguationData":[TD([[makeQuery(id+"F55.imprint","IMPRINT",EDGE,{"derivedFrom":sQuery(id+"F55.wireOp",EDGE,"E134.bottom")}),-1.0]])]});
            extrude(context, id + "F56", {"entities" : qUnion([Q0]), "operationType" : NewBodyOperationType.REMOVE, "endBound" : BoundingType.THROUGH_ALL, "oppositeDirection" : true, "depth" : 25.4 * mm, "offsetDistance" : 25.4 * mm, "hasSecondDirection" : true, "secondDirectionBound" : SecondDirectionBoundingType.THROUGH_ALL, "secondDirectionOppositeDirection" : false, "secondDirectionDepth" : 25.4 * mm});
        }
        {
            var Q0;
            Q0=sQuery(id+"F6.wireOp",VERTEX,"E49.end");
            var Q1;
            Q1=sQuery(id+"F4.wireOp",VERTEX,"E26.start");
            var Q2;
            Q2=sQuery(id+"F4.wireOp",VERTEX,"E26.end");
            cPlane(context, id + "F57", {"entities" : qUnion([Q0, Q1, Q2]), "cplaneType" : CPlaneType.THREE_POINT, "offset" : 25.4 * mm, "width" : 152.4 * mm, "height" : 152.4 * mm});
        }
        {
            var Q0;
            Q0=qCreatedBy(id+"F57.planeOp",FACE);
            var sketch = newSketch(context, id + "F58", { "sketchPlane" : qUnion([Q0])});
            skLineSegment(sketch, "E136.bottom", {"start": v(51.37, 31.75) * mm, "end": v(71, 31.75) * mm});
            skLineSegment(sketch, "E136.top", {"start": v(51.37, -31.75) * mm, "end": v(71, -31.75) * mm});
            skLineSegment(sketch, "E136.left", {"start": v(51.37, 31.75) * mm, "end": v(51.37, -31.75) * mm});
            skLineSegment(sketch, "E136.right", {"start": v(71, 31.75) * mm, "end": v(71, -31.75) * mm});
            skLineSegment(sketch, "E137", {"start": v(51.37, 31.75) * mm, "end": v(63.5, -31.75) * mm});
            skSolve(sketch);
        }
        {
            var Q0;
            Q0=makeQuery(id+"F58.imprint","IMPRINT",FACE,{"disambiguationData":[TD([[makeQuery(id+"F58.imprint","IMPRINT",EDGE,{"derivedFrom":sQuery(id+"F58.wireOp",EDGE,"E136.bottom")}),-1.0]])]});
            extrude(context, id + "F59", {"entities" : qUnion([Q0]), "operationType" : NewBodyOperationType.REMOVE, "endBound" : BoundingType.THROUGH_ALL, "oppositeDirection" : true, "depth" : 25.4 * mm, "offsetDistance" : 25.4 * mm, "hasSecondDirection" : true, "secondDirectionBound" : SecondDirectionBoundingType.THROUGH_ALL, "secondDirectionOppositeDirection" : false, "secondDirectionDepth" : 25.4 * mm});
        }
        {
            var Q0;
            Q0=sQuery(id+"F4.wireOp",VERTEX,"E41.start");
            var Q1;
            Q1=sQuery(id+"F7.wireOp",VERTEX,"E75.end");
            var Q2;
            Q2=sQuery(id+"F4.wireOp",VERTEX,"E38.start");
            cPlane(context, id + "F60", {"entities" : qUnion([Q0, Q1, Q2]), "cplaneType" : CPlaneType.THREE_POINT, "offset" : 25.4 * mm, "width" : 152.4 * mm, "height" : 152.4 * mm});
        }
        {
            var Q0;
            Q0=qCreatedBy(id+"F60.planeOp",FACE);
            var sketch = newSketch(context, id + "F61", { "sketchPlane" : qUnion([Q0])});
            skLineSegment(sketch, "E138", {"start": v(0, 71) * mm, "end": v(51.37, 31.75) * mm});
            skLineSegment(sketch, "E139", {"start": v(0, 71) * mm, "end": v(63.5, 71) * mm});
            skLineSegment(sketch, "E140", {"start": v(63.5, 71) * mm, "end": v(63.5, 31.75) * mm});
            skLineSegment(sketch, "E141", {"start": v(63.5, 31.75) * mm, "end": v(51.37, 31.75) * mm});
            skSolve(sketch);
        }
        {
            var Q0;
            {var subQ0=sQuery(id+"F61.wireOp",EDGE,"E138");Q0=makeQuery(id+"F61.imprint","IMPRINT",FACE,{"disambiguationData":[TD([[makeQuery(id+"F61.imprint","IMPRINT",EDGE,{"derivedFrom":subQ0}),1.0]])]});}
            var Q1;
            Q1=sQuery(id+"F4.wireOp",VERTEX,"E21.end");
            var Q2;
            Q2=sQuery(id+"F4.wireOp",VERTEX,"E22.end");
            extrude(context, id + "F62", {"entities" : qUnion([Q0]), "operationType" : NewBodyOperationType.REMOVE, "endBound" : BoundingType.UP_TO_VERTEX, "depth" : 25.4 * mm, "endBoundEntityVertex" : qUnion([Q1]), "offsetDistance" : 25.4 * mm, "hasSecondDirection" : true, "secondDirectionBound" : SecondDirectionBoundingType.UP_TO_VERTEX, "secondDirectionOppositeDirection" : true, "secondDirectionDepth" : 25.4 * mm, "secondDirectionBoundEntityVertex" : qUnion([Q2])});
        }
        {
            var Q0;
            Q0=sQuery(id+"F7.wireOp",VERTEX,"E75.end");
            var Q1;
            Q1=sQuery(id+"F4.wireOp",VERTEX,"E41.start");
            var Q2;
            Q2=sQuery(id+"F4.wireOp",VERTEX,"E26.end");
            cPlane(context, id + "F63", {"entities" : qUnion([Q0, Q1, Q2]), "cplaneType" : CPlaneType.THREE_POINT, "offset" : 25.4 * mm, "width" : 152.4 * mm, "height" : 152.4 * mm});
        }
        {
            var Q0;
            Q0=qCreatedBy(id+"F63.planeOp",FACE);
            var sketch = newSketch(context, id + "F64", { "sketchPlane" : qUnion([Q0])});
            skLineSegment(sketch, "E142", {"start": v(0, 71) * mm, "end": v(-51.37, 31.75) * mm});
            skLineSegment(sketch, "E143", {"start": v(0, 71) * mm, "end": v(-63.5, 71) * mm});
            skLineSegment(sketch, "E144", {"start": v(-63.5, 71) * mm, "end": v(-63.5, 31.75) * mm});
            skLineSegment(sketch, "E145", {"start": v(-63.5, 31.75) * mm, "end": v(-51.37, 31.75) * mm});
            skSolve(sketch);
        }
        {
            var Q0;
            Q0=makeQuery(id+"F64.imprint","IMPRINT",FACE,{"disambiguationData":[TD([[makeQuery(id+"F64.imprint","IMPRINT",EDGE,{"derivedFrom":sQuery(id+"F64.wireOp",EDGE,"E142")}),-1.0]])]});
            extrude(context, id + "F65", {"entities" : qUnion([Q0]), "operationType" : NewBodyOperationType.REMOVE, "endBound" : BoundingType.THROUGH_ALL, "oppositeDirection" : true, "depth" : 25.4 * mm, "offsetDistance" : 25.4 * mm, "hasSecondDirection" : true, "secondDirectionBound" : SecondDirectionBoundingType.THROUGH_ALL, "secondDirectionOppositeDirection" : false, "secondDirectionDepth" : 25.4 * mm});
        }
        {
            var Q0;
            Q0=sQuery(id+"F7.wireOp",VERTEX,"E75.end");
            var Q1;
            Q1=sQuery(id+"F4.wireOp",VERTEX,"E41.start");
            var Q2;
            Q2=sQuery(id+"F4.wireOp",VERTEX,"E33.end");
            cPlane(context, id + "F66", {"entities" : qUnion([Q0, Q1, Q2]), "cplaneType" : CPlaneType.THREE_POINT, "offset" : 25.4 * mm, "width" : 152.4 * mm, "height" : 152.4 * mm});
        }
        {
            var Q0;
            Q0=qCreatedBy(id+"F66.planeOp",FACE);
            var sketch = newSketch(context, id + "F67", { "sketchPlane" : qUnion([Q0])});
            skLineSegment(sketch, "E146", {"start": v(0, 71) * mm, "end": v(-51.37, 31.75) * mm});
            skLineSegment(sketch, "E147", {"start": v(0, 71) * mm, "end": v(-63.5, 71) * mm});
            skLineSegment(sketch, "E148", {"start": v(-63.5, 71) * mm, "end": v(-63.5, 31.75) * mm});
            skLineSegment(sketch, "E149", {"start": v(-63.5, 31.75) * mm, "end": v(-51.37, 31.75) * mm});
            skSolve(sketch);
        }
        {
            var Q0;
            {var subQ0=sQuery(id+"F67.wireOp",EDGE,"E146");Q0=makeQuery(id+"F67.imprint","IMPRINT",FACE,{"disambiguationData":[TD([[makeQuery(id+"F67.imprint","IMPRINT",EDGE,{"derivedFrom":subQ0}),-1.0]])]});}
            extrude(context, id + "F68", {"entities" : qUnion([Q0]), "operationType" : NewBodyOperationType.REMOVE, "endBound" : BoundingType.THROUGH_ALL, "oppositeDirection" : true, "depth" : 25.4 * mm, "offsetDistance" : 25.4 * mm, "hasSecondDirection" : true, "secondDirectionBound" : SecondDirectionBoundingType.THROUGH_ALL, "secondDirectionOppositeDirection" : false, "secondDirectionDepth" : 25.4 * mm});
        }
        {
            var Q0;
            Q0=sQuery(id+"F4.wireOp",VERTEX,"E30.end");
            var Q1;
            Q1=sQuery(id+"F4.wireOp",VERTEX,"E41.start");
            var Q2;
            Q2=sQuery(id+"F7.wireOp",VERTEX,"E75.end");
            cPlane(context, id + "F69", {"entities" : qUnion([Q0, Q1, Q2]), "cplaneType" : CPlaneType.THREE_POINT, "offset" : 25.4 * mm, "width" : 152.4 * mm, "height" : 152.4 * mm});
        }
        {
            var Q0;
            Q0=qCreatedBy(id+"F69.planeOp",FACE);
            var sketch = newSketch(context, id + "F70", { "sketchPlane" : qUnion([Q0])});
            skLineSegment(sketch, "E150", {"start": v(0, 71) * mm, "end": v(51.37, 31.75) * mm});
            skLineSegment(sketch, "E151", {"start": v(0, 71) * mm, "end": v(63.5, 71) * mm});
            skLineSegment(sketch, "E152", {"start": v(63.5, 71) * mm, "end": v(63.5, 31.75) * mm});
            skLineSegment(sketch, "E153", {"start": v(63.5, 31.75) * mm, "end": v(51.37, 31.75) * mm});
            skSolve(sketch);
        }
        {
            var Q0;
            Q0=makeQuery(id+"F70.imprint","IMPRINT",FACE,{"disambiguationData":[TD([[makeQuery(id+"F70.imprint","IMPRINT",EDGE,{"derivedFrom":sQuery(id+"F70.wireOp",EDGE,"E150")}),1.0]])]});
            extrude(context, id + "F71", {"entities" : qUnion([Q0]), "operationType" : NewBodyOperationType.REMOVE, "endBound" : BoundingType.THROUGH_ALL, "oppositeDirection" : true, "depth" : 25.4 * mm, "offsetDistance" : 25.4 * mm, "hasSecondDirection" : true, "secondDirectionBound" : SecondDirectionBoundingType.THROUGH_ALL, "secondDirectionOppositeDirection" : false, "secondDirectionDepth" : 25.4 * mm});
        }
        {
            var Q0;
            Q0=sQuery(id+"F4.wireOp",VERTEX,"E27.end");
            var Q1;
            Q1=sQuery(id+"F4.wireOp",VERTEX,"E41.start");
            var Q2;
            Q2=sQuery(id+"F7.wireOp",VERTEX,"E75.end");
            cPlane(context, id + "F72", {"entities" : qUnion([Q0, Q1, Q2]), "cplaneType" : CPlaneType.THREE_POINT, "offset" : 25.4 * mm, "width" : 152.4 * mm, "height" : 152.4 * mm});
        }
        {
            var Q0;
            Q0=qCreatedBy(id+"F72.planeOp",FACE);
            var sketch = newSketch(context, id + "F73", { "sketchPlane" : qUnion([Q0])});
            skLineSegment(sketch, "E154", {"start": v(0, 71) * mm, "end": v(51.37, 31.75) * mm});
            skLineSegment(sketch, "E155", {"start": v(0, 71) * mm, "end": v(63.5, 71) * mm});
            skLineSegment(sketch, "E156", {"start": v(63.5, 71) * mm, "end": v(63.5, 31.75) * mm});
            skLineSegment(sketch, "E157", {"start": v(63.5, 31.75) * mm, "end": v(51.37, 31.75) * mm});
            skSolve(sketch);
        }
        {
            var Q0;
            {var subQ0=sQuery(id+"F73.wireOp",EDGE,"E154");Q0=makeQuery(id+"F73.imprint","IMPRINT",FACE,{"disambiguationData":[TD([[makeQuery(id+"F73.imprint","IMPRINT",EDGE,{"derivedFrom":subQ0}),1.0]])]});}
            extrude(context, id + "F74", {"entities" : qUnion([Q0]), "operationType" : NewBodyOperationType.REMOVE, "endBound" : BoundingType.THROUGH_ALL, "oppositeDirection" : true, "depth" : 25.4 * mm, "offsetDistance" : 25.4 * mm, "hasSecondDirection" : true, "secondDirectionBound" : SecondDirectionBoundingType.THROUGH_ALL, "secondDirectionOppositeDirection" : false, "secondDirectionDepth" : 25.4 * mm});
        }
    });
